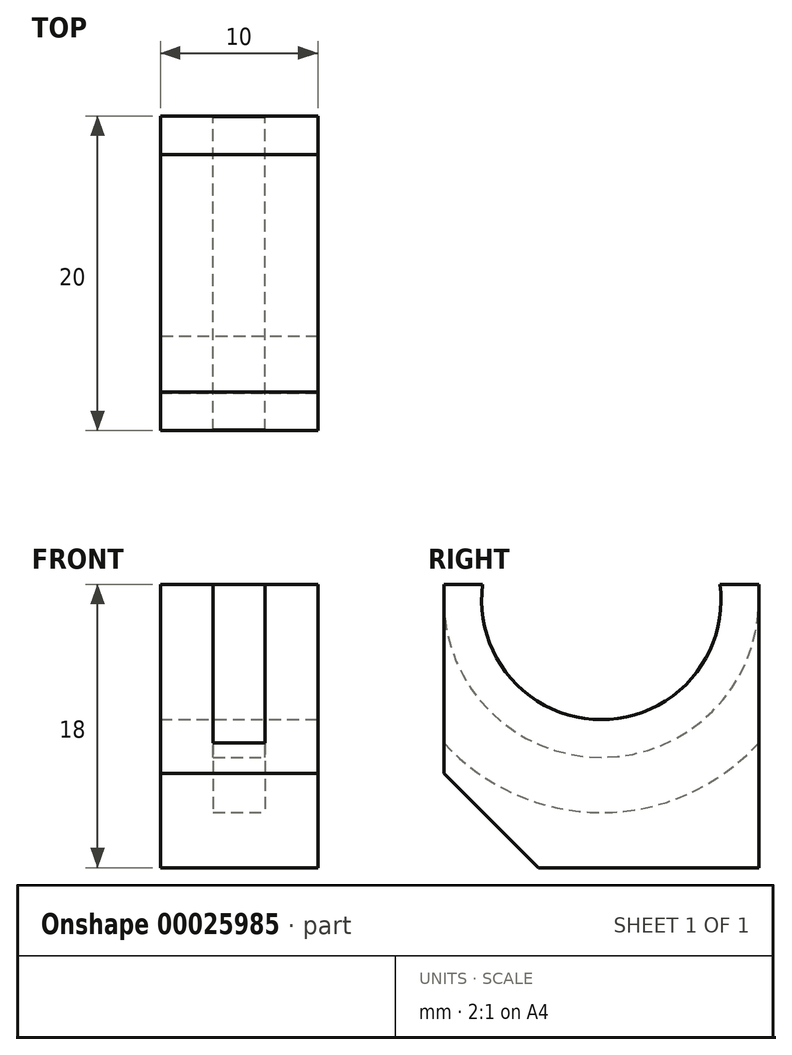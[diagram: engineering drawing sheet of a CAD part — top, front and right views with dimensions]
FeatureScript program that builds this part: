
annotation { "Feature Type Name" : "Feature", "Feature Type Description" : "" }
export const myFeature = defineFeature(function(context is Context, id is Id, definition is map)
    precondition{}
    {
        {
            var Q0;
            Q0=qCreatedBy(makeId("Top.planeOp"),FACE);
            var sketch = newSketch(context, id + "F0", { "sketchPlane" : qUnion([Q0])});
            skLineSegment(sketch, "E0.bottom", {"start": v(0, 0) * mm, "end": v(10, 0) * mm});
            skLineSegment(sketch, "E0.top", {"start": v(0, 20) * mm, "end": v(10, 20) * mm});
            skLineSegment(sketch, "E0.left", {"start": v(0, 0) * mm, "end": v(0, 20) * mm});
            skLineSegment(sketch, "E0.right", {"start": v(10, 0) * mm, "end": v(10, 20) * mm});
            skSolve(sketch);
        }
        {
            var Q0;
            Q0=makeQuery(id+"F0.imprint","IMPRINT",FACE,{"disambiguationData":[TD([[makeQuery(id+"F0.imprint","IMPRINT",EDGE,{"derivedFrom":sQuery(id+"F0.wireOp",EDGE,"E0.bottom")}),1.0]])]});
            extrude(context, id + "F1", {"entities" : qUnion([Q0]), "depth" : 18 * mm});
        }
        {
            var Q0;
            Q0=makeQuery(id+"F1.opExtrude","SWEPT_FACE",FACE,{"disambiguationData":[OSD([sQuery(id+"F0.wireOp",EDGE,"E0.right")])]});
            var sketch = newSketch(context, id + "F2", { "sketchPlane" : qUnion([Q0])});
            skCircle(sketch, "E1", {"center": v(10, 17) * mm, "radius": 7.6 * mm});
            skPoint(sketch, "E1.centerSnap0", {"position": v(10, 18) * mm});
            skSolve(sketch);
        }
        {
            var Q0;
            Q0 = qSketchRegion(id + "F2", true);
            extrude(context, id + "F3", {"entities" : qUnion([Q0]), "operationType" : NewBodyOperationType.REMOVE, "endBound" : BoundingType.THROUGH_ALL, "oppositeDirection" : true, "depth" : 25 * mm});
        }
        {
            var Q0;
            Q0=makeQuery(id+"F1.opExtrude","SWEPT_FACE",FACE,{"disambiguationData":[OSD([sQuery(id+"F0.wireOp",EDGE,"E0.right")])]});
            var Q1;
            Q1=makeQuery(id+"F1.opExtrude","SWEPT_FACE",FACE,{"disambiguationData":[OSD([sQuery(id+"F0.wireOp",EDGE,"E0.left")])]});
            cPlane(context, id + "F4", {"entities" : qUnion([Q0, Q1]), "cplaneType" : CPlaneType.MID_PLANE, "offset" : 150 * mm, "width" : 150 * mm, "height" : 150 * mm});
        }
        {
            var Q0;
            Q0=qCreatedBy(id+"F4.planeOp",FACE);
            var sketch = newSketch(context, id + "F5", { "sketchPlane" : qUnion([Q0])});
            skArc(sketch, "E2.0", {"start": v(2.47, 18) * mm, "mid": v(10, 9.4) * mm, "end": v(17.53, 18) * mm});
            skCircle(sketch, "E3", {"center": v(10, 17) * mm, "radius": 10 * mm});
            skCircle(sketch, "E4.0", {"center": v(10, 17) * mm, "radius": 13.5 * mm});
            skSolve(sketch);
        }
        {
            var Q0;
            Q0=makeQuery(id+"F5.imprint","IMPRINT",FACE,{"disambiguationData":[TD([[makeQuery(id+"F5.imprint","IMPRINT",EDGE,{"derivedFrom":sQuery(id+"F5.wireOp",EDGE,"E3")}),-1.0]])]});
            extrude(context, id + "F6", {"entities" : qUnion([Q0]), "operationType" : NewBodyOperationType.REMOVE, "endBound" : BoundingType.SYMMETRIC, "oppositeDirection" : true, "depth" : 3.3 * mm});
        }
        {
            var Q0;
            Q0=makeQuery(id+"F1.opExtrude","CAP_EDGE",EDGE,{"disambiguationData":[OSD([sQuery(id+"F0.wireOp",EDGE,"E0.bottom")])],"isStart":true});
            chamfer(context, id + "F7", {"entities" : qUnion([Q0]), "width" : 6 * mm, "tangentPropagation" : true});
        }
    });
